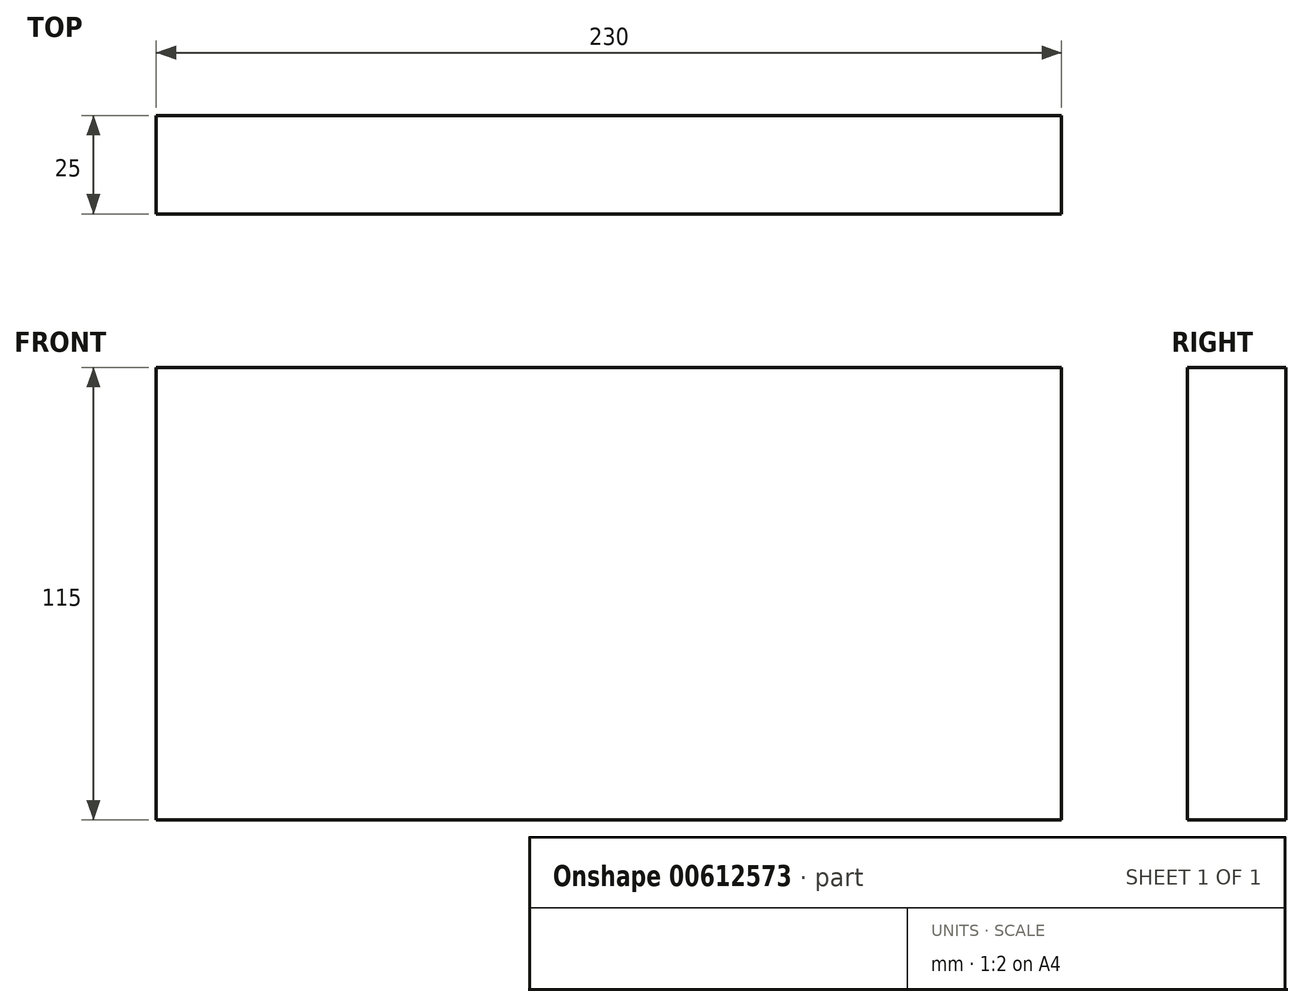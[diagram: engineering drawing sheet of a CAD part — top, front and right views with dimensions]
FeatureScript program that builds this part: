
annotation { "Feature Type Name" : "Feature", "Feature Type Description" : "" }
export const myFeature = defineFeature(function(context is Context, id is Id, definition is map)
    precondition{}
    {
        {
            var Q0;
            Q0=qCreatedBy(makeId("Front.planeOp"),FACE);
            var sketch = newSketch(context, id + "F0", { "sketchPlane" : qUnion([Q0])});
            skLineSegment(sketch, "E0.bottom", {"start": v(-115, -57.5) * mm, "end": v(115, -57.5) * mm});
            skLineSegment(sketch, "E0.top", {"start": v(-115, 57.5) * mm, "end": v(115, 57.5) * mm});
            skLineSegment(sketch, "E0.left", {"start": v(-115, -57.5) * mm, "end": v(-115, 57.5) * mm});
            skLineSegment(sketch, "E0.right", {"start": v(115, -57.5) * mm, "end": v(115, 57.5) * mm});
            skPoint(sketch, "E0.middle", {"position": v(0, 0) * mm});
            skSolve(sketch);
        }
        {
            var Q0;
            Q0=makeQuery(id+"F0.imprint","IMPRINT",FACE,{"disambiguationData":[TD([[makeQuery(id+"F0.imprint","IMPRINT",EDGE,{"derivedFrom":sQuery(id+"F0.wireOp",EDGE,"E0.bottom")}),1.0]])]});
            extrude(context, id + "F1", {"entities" : qUnion([Q0]), "depth" : 25 * mm, "offsetDistance" : 25.4 * mm});
        }
    });
